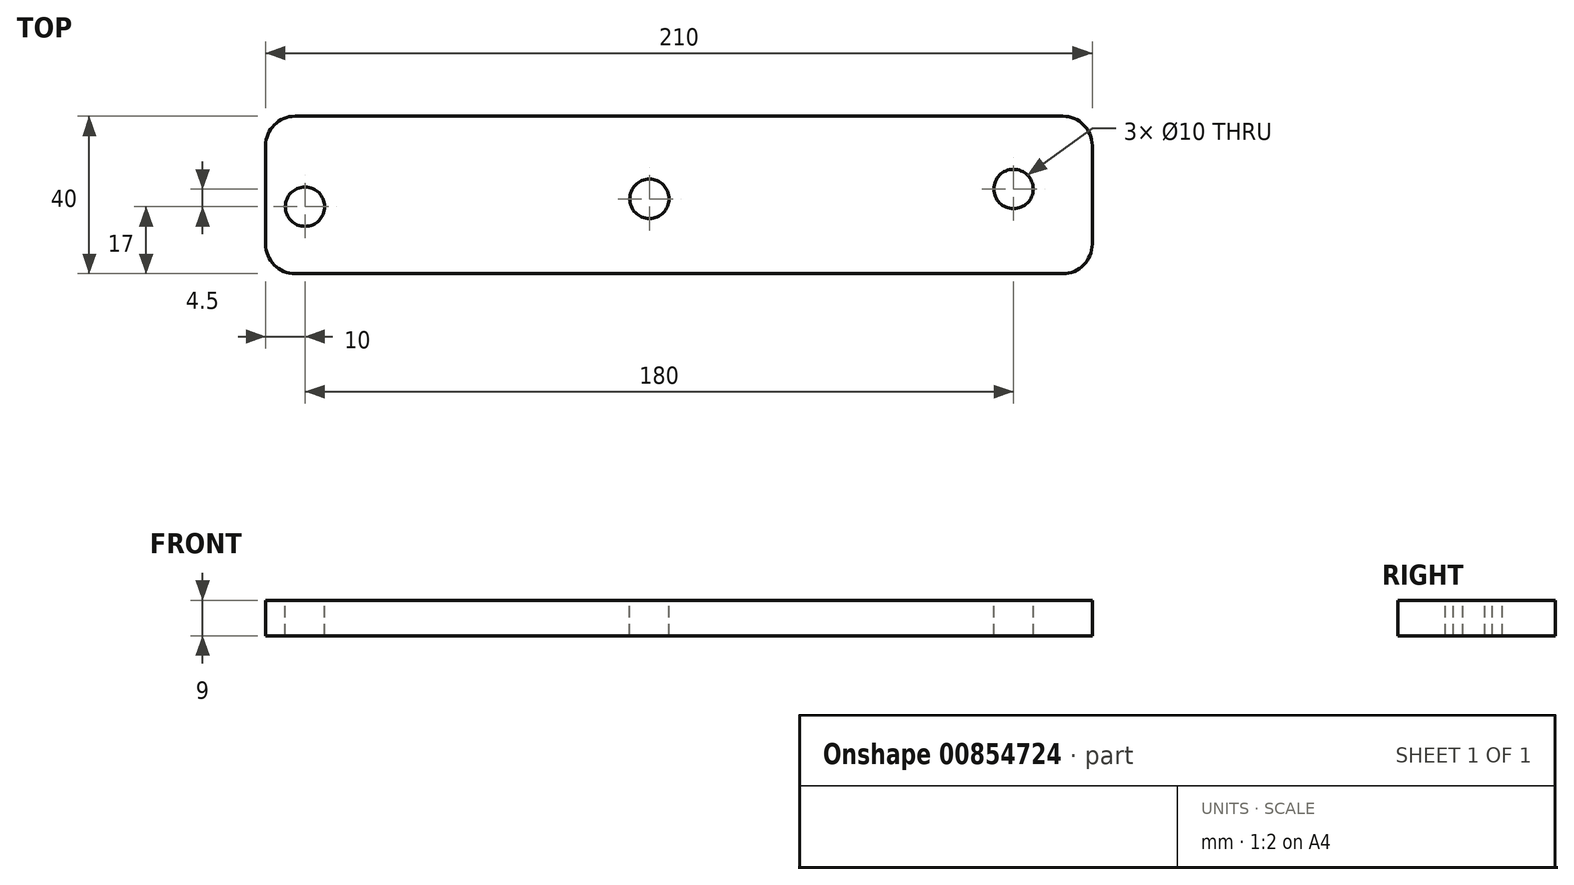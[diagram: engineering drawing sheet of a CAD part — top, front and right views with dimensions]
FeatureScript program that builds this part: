
annotation { "Feature Type Name" : "Feature", "Feature Type Description" : "" }
export const myFeature = defineFeature(function(context is Context, id is Id, definition is map)
    precondition{}
    {
        {
            var Q0;
            Q0=qCreatedBy(makeId("Top.planeOp"),FACE);
            var sketch = newSketch(context, id + "F0", { "sketchPlane" : qUnion([Q0])});
            skLineSegment(sketch, "E0.bottom", {"start": v(-105, 22.5) * mm, "end": v(105, 22.5) * mm});
            skLineSegment(sketch, "E0.top", {"start": v(-105, -22.5) * mm, "end": v(105, -22.5) * mm});
            skLineSegment(sketch, "E0.left", {"start": v(-105, 22.5) * mm, "end": v(-105, -22.5) * mm});
            skLineSegment(sketch, "E0.right", {"start": v(105, 22.5) * mm, "end": v(105, -22.5) * mm});
            skPoint(sketch, "E0.middle", {"position": v(0, 0) * mm});
            skPoint(sketch, "E1", {"position": v(85, 4) * mm});
            skPoint(sketch, "E2", {"position": v(-7.5, 1.5) * mm});
            skPoint(sketch, "E3", {"position": v(-95, -0.5) * mm});
            skLineSegment(sketch, "E4", {"start": v(-105, -17.5) * mm, "end": v(105, -17.5) * mm});
            skSolve(sketch);
        }
        {
            var Q0;
            Q0=makeQuery(id+"F0.imprint","IMPRINT",FACE,{"disambiguationData":[TD([[makeQuery(id+"F0.imprint","IMPRINT",EDGE,{"derivedFrom":sQuery(id+"F0.wireOp",EDGE,"E0.bottom")}),-1.0]])]});
            extrude(context, id + "F1", {"entities" : qUnion([Q0]), "depth" : 9 * mm, "offsetDistance" : 25 * mm});
        }
        {
            var Q0;
            Q0=sQuery(id+"F0.wireOp",VERTEX,"E3");
            var Q1;
            Q1=sQuery(id+"F0.wireOp",VERTEX,"E2");
            var Q2;
            Q2=sQuery(id+"F0.wireOp",VERTEX,"E1");
            var Q3;
            Q3=makeQuery(id+"F1.opExtrude","SWEPT_BODY",BODY,{"disambiguationData":[OSD([sQuery(id+"F0.wireOp",EDGE,"E0.bottom"),sQuery(id+"F0.wireOp",EDGE,"E0.top"),sQuery(id+"F0.wireOp",EDGE,"E0.left"),sQuery(id+"F0.wireOp",EDGE,"E0.right")])]});
            hole(context, id + "F2", {"style" : HoleStyle.SIMPLE, "endStyle" : HoleEndStyle.THROUGH, "oppositeDirection" : true, "holeDiameter" : 10 * mm, "majorDiameter" : 5 * mm, "isTappedThrough" : true, "tappedDepth" : 12 * mm, "tapClearance" : 3, "locations" : qUnion([Q0, Q1, Q2]), "scope" : qUnion([Q3]), "startStyle" : HoleStartStyle.SKETCH});
        }
        {
            var Q0;
            Q0=makeQuery(id+"F1.opExtrude","SWEPT_EDGE",EDGE,{"disambiguationData":[OSD([sQuery(id+"F0.wireOp",EDGE,"E0.bottom"),sQuery(id+"F0.wireOp",EDGE,"E0.left")])]});
            var Q1;
            Q1=makeQuery(id+"F1.opExtrude","SWEPT_EDGE",EDGE,{"disambiguationData":[OSD([sQuery(id+"F0.wireOp",EDGE,"E0.top"),sQuery(id+"F0.wireOp",EDGE,"E0.left")])]});
            var Q2;
            Q2=makeQuery(id+"F1.opExtrude","SWEPT_EDGE",EDGE,{"disambiguationData":[OSD([sQuery(id+"F0.wireOp",EDGE,"E0.bottom"),sQuery(id+"F0.wireOp",EDGE,"E0.right")])]});
            var Q3;
            Q3=makeQuery(id+"F1.opExtrude","SWEPT_EDGE",EDGE,{"disambiguationData":[OSD([sQuery(id+"F0.wireOp",EDGE,"E0.top"),sQuery(id+"F0.wireOp",EDGE,"E0.right")])]});
            fillet(context, id + "F3", {"entities" : qUnion([Q0, Q1, Q2, Q3]), "radius" : 7.5 * mm, "tangentPropagation" : true, "allowEdgeOverflow" : false});
        }
    });
